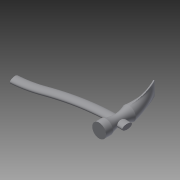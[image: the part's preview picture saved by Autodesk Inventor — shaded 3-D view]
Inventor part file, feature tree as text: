
AUTODESK INVENTOR PART (.ipt)
format: ipt  version: 2015 SP2 (Build 190223200, 223)  size: 225,280 bytes
history: native  units: mm
features: sketch x7, other x5, plane x4, loft x2, sweep x1
ambient origin geometry x8: Origin, YZ Plane, XZ Plane, XY Plane, X Axis, Y Axis, Z Axis, Center Point
bodies: Volumenkörper1 (feature_tree)
feature tree (19):
  other  "Verdickung1"
  plane  "Arbeitsebene1"
  sketch  "Skizze2"  dims[d4=3.0mm d5=5.0mm d6=5.0mm]
  plane  "Arbeitsebene2"
  sketch  "Skizze3"  dims[d7=4.0mm d8=5.0mm]
  loft  "Erhebung1"
  plane  "Arbeitsebene3"
  loft  "Erhebung3"
  sketch  "Skizze6"  dims[d12=0.0mm d13=90.0deg]
  plane  "Arbeitsebene4"
  sweep  "Sweeping1"
  sketch  "Skizze1"  dims[d2=3.0mm d3=90.0deg]
  other  "Fläche1"
  other  "Kanten1"
  sketch  "Skizze4"  dims[d9=6.0mm]
  sketch  "Skizze5"  dims[d10=0.0mm d11=90.0deg]
  other  "Kanten2"
  sketch  "Skizze7"  dims[d14=0.0mm d15=90.0deg d16=15.0mm d17=0.5mm d18=6.0mm d23=0.0mm d24=90.0deg d25=0.0mm d26=90.0deg d27=0.0mm d28=90.0deg d29=0.0mm d30=0.0mm d31=0.0mm]
  other  "Rotationsfläche1"
